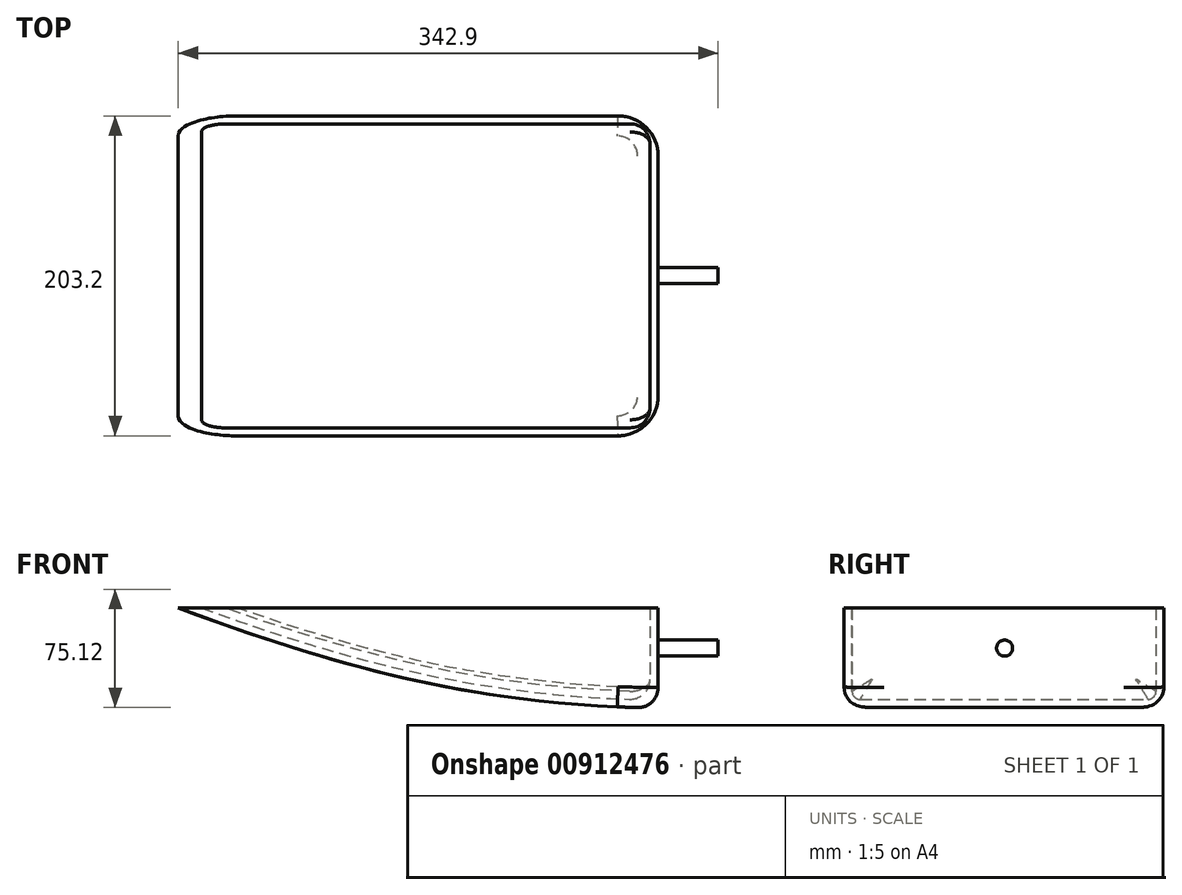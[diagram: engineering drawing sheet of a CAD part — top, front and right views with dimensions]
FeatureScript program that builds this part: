
annotation { "Feature Type Name" : "Feature", "Feature Type Description" : "" }
export const myFeature = defineFeature(function(context is Context, id is Id, definition is map)
    precondition{}
    {
        {
            var Q0;
            Q0=qCreatedBy(makeId("Front.planeOp"),FACE);
            var sketch = newSketch(context, id + "F0", { "sketchPlane" : qUnion([Q0])});
            skLineSegment(sketch, "E0", {"start": v(-107.45, 9.01) * mm, "end": v(197.35, 9.01) * mm});
            skLineSegment(sketch, "E1", {"start": v(197.35, 9.01) * mm, "end": v(197.35, -54.49) * mm});
            skFitSpline(sketch, "E2", {"points": [v(-107.45, 9.01) * mm, v(197.35, -54.49) * mm], "startDerivative": vector(322.35, -118.75) * mm, "endDerivative": vector(340.21, -5.38) * mm});
            skLineSegment(sketch, "E3.filletArc", {"start": v(197.35, -54.49) * mm, "end": v(197.35, -54.49) * mm});
            skPoint(sketch, "E4.visualSharp", {"position": v(197.35, 9.01) * mm});
            skLineSegment(sketch, "E4.filletArc", {"start": v(197.35, 9.01) * mm, "end": v(197.35, 9.01) * mm});
            skSolve(sketch);
        }
        {
            var Q0;
            Q0=makeQuery(id+"F0.imprint","IMPRINT",FACE,{"disambiguationData":[TD([[makeQuery(id+"F0.imprint","IMPRINT",EDGE,{"derivedFrom":sQuery(id+"F0.wireOp",EDGE,"E0")}),-1.0]])]});
            extrude(context, id + "F1", {"entities" : qUnion([Q0]), "depth" : 203.2 * mm, "offsetDistance" : 25.4 * mm});
        }
        {
            var Q0;
            Q0=makeQuery(id+"F1.opExtrude","SWEPT_FACE",FACE,{"disambiguationData":[OSD([sQuery(id+"F0.wireOp",EDGE,"E0")])]});
            shell(context, id + "F2", {"entities" : qUnion([Q0]), "thickness" : 5.08 * mm});
        }
        {
            var Q0;
            Q0=makeQuery(id+"F1.opExtrude","SWEPT_FACE",FACE,{"disambiguationData":[OSD([sQuery(id+"F0.wireOp",EDGE,"E1")])]});
            var sketch = newSketch(context, id + "F3", { "sketchPlane" : qUnion([Q0])});
            skCircle(sketch, "E5", {"center": v(-101.25, -16.38) * mm, "radius": 5.08 * mm});
            skSolve(sketch);
        }
        {
            var Q0;
            Q0 = qSketchRegion(id + "F3", true);
            extrude(context, id + "F4", {"entities" : qUnion([Q0]), "operationType" : NewBodyOperationType.ADD, "depth" : 38.1 * mm, "offsetDistance" : 25.4 * mm});
        }
        {
            var Q0;
            Q0=makeQuery(id+"F1.opExtrude","SWEPT_EDGE",EDGE,{"disambiguationData":[OSD([sQuery(id+"F0.wireOp",EDGE,"E1"),sQuery(id+"F0.wireOp",EDGE,"E2")])]});
            var Q1;
            Q1=makeQuery(id+"F1.opExtrude","CAP_EDGE",EDGE,{"disambiguationData":[OSD([sQuery(id+"F0.wireOp",EDGE,"E2")])],"isStart":true});
            var Q2;
            Q2=makeQuery(id+"F1.opExtrude","CAP_EDGE",EDGE,{"disambiguationData":[OSD([sQuery(id+"F0.wireOp",EDGE,"E2")])],"isStart":false});
            fillet(context, id + "F5", {"entities" : qUnion([Q0, Q1, Q2]), "radius" : 12.7 * mm, "tangentPropagation" : true, "allowEdgeOverflow" : false});
        }
        {
            var Q0;
            {var subQ0=sQuery(id+"F0.wireOp",EDGE,"E2");Q0=makeQuery(id+"F2.opShell","OFFSET_EDGE",EDGE,{"disambiguationData":[OSD([subQ0]),TDD([makeQuery(id+"F1.opExtrude","CAP_EDGE",EDGE,{"disambiguationData":[OSD([subQ0])],"isStart":true})])]});}
            fillet(context, id + "F6", {"entities" : qUnion([Q0]), "radius" : 5.08 * mm, "tangentPropagation" : true, "allowEdgeOverflow" : false});
        }
        {
            var Q0;
            {var subQ0=sQuery(id+"F0.wireOp",EDGE,"E2");Q0=makeQuery(id+"F2.opShell","OFFSET_EDGE",EDGE,{"disambiguationData":[OSD([subQ0]),TDD([makeQuery(id+"F1.opExtrude","CAP_EDGE",EDGE,{"disambiguationData":[OSD([subQ0])],"isStart":false})])]});}
            fillet(context, id + "F7", {"entities" : qUnion([Q0]), "radius" : 5.08 * mm, "tangentPropagation" : true, "allowEdgeOverflow" : false});
        }
        {
            var Q0;
            Q0=makeQuery(id+"F2.opShell","OFFSET_EDGE",EDGE,{"disambiguationData":[OSD([sQuery(id+"F0.wireOp",EDGE,"E1"),sQuery(id+"F0.wireOp",EDGE,"E2")])]});
            fillet(context, id + "F8", {"entities" : qUnion([Q0]), "radius" : 12.7 * mm, "tangentPropagation" : true, "allowEdgeOverflow" : false});
        }
        {
            var Q0;
            Q0=makeQuery(id+"F1.opExtrude","CAP_EDGE",EDGE,{"disambiguationData":[OSD([sQuery(id+"F0.wireOp",EDGE,"E1")])],"isStart":true});
            var Q1;
            Q1=makeQuery(id+"F1.opExtrude","CAP_EDGE",EDGE,{"disambiguationData":[OSD([sQuery(id+"F0.wireOp",EDGE,"E1")])],"isStart":false});
            fillet(context, id + "F9", {"entities" : qUnion([Q0, Q1]), "radius" : 25.4 * mm, "tangentPropagation" : true, "allowEdgeOverflow" : false});
        }
    });
